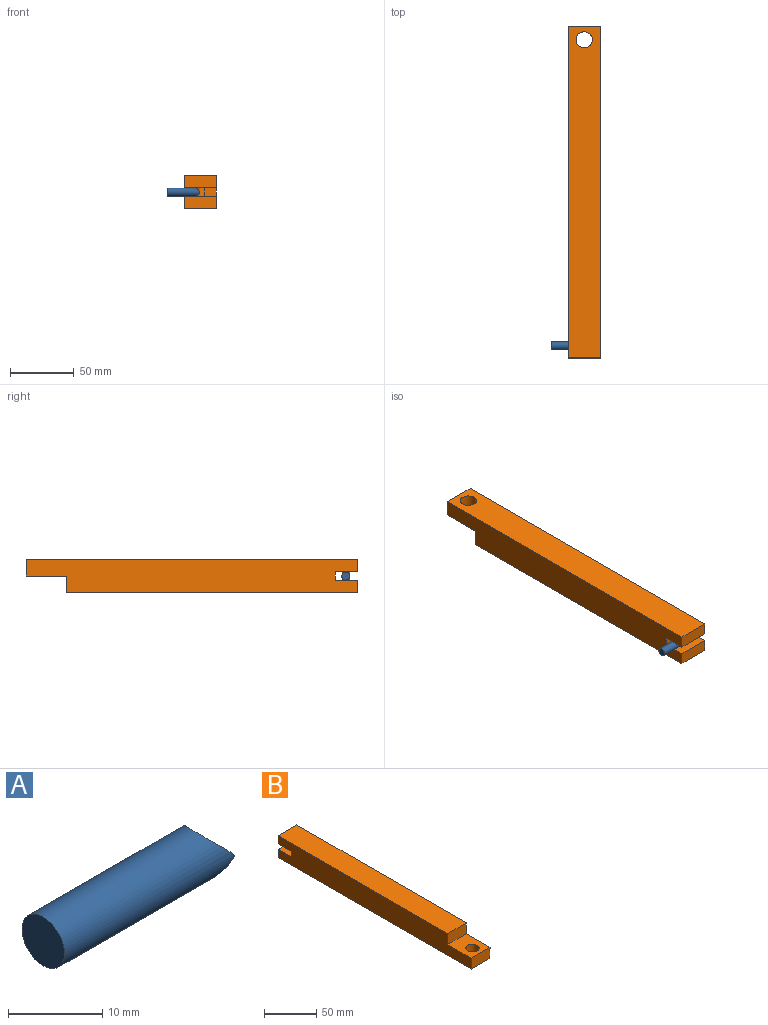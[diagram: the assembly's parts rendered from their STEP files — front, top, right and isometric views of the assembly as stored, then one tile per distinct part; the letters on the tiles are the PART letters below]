
ASSEMBLY  parts=2 mates=1
PART A: 5 faces, bbox 25.4x6.4x6.4 mm
  f0: plane 0.4x0.01mm, normal (1,0,0), area 0mm2, adj f1,f4
  f1: cylinder r=3.17mm len=25.4mm, axis (-1,0,0), area 470.3mm2, adj f0,f2,f3,f4
  f2: plane 0.4x0.01mm, normal (1,0,0), area 0mm2, adj f1,f4
  f3: plane 6.35x6.35mm, normal (-1,0,0), area 31.7mm2, adj f1
  f4: cylinder r=3.17mm len=6.35mm, axis (0,0,1), area 40.2mm2, adj f0,f1,f2
PART B: 14 faces, bbox 25.4x260.4x25.4 mm
  f0: plane 228.6x25.4mm, normal (0,0,1), area 5806.4mm2, adj f1,f2,f4,f10
  f1: plane 260.35x25.4mm, normal (1,0,0), area 6097.7mm2, adj f0,f3,f4,f5,f6,f7,f8,f9
  f2: plane 260.35x25.4mm, normal (-1,0,0), area 6097.7mm2, adj f0,f3,f4,f5,f6,f7,f8,f9
  f3: plane 25.4x17.64mm, normal (0,0,-1), area 416.3mm2, adj f1,f2,f4,f9,f12
  f4: plane 25.4x9.53mm, normal (0,1,0), area 241.9mm2, adj f0,f1,f2,f3
  f5: plane 25.4x12.7mm, normal (0,-1,0), area 322.6mm2, adj f1,f2,f6,f11
  f6: plane 260.35x25.4mm, normal (0,0,-1), area 6486.2mm2, adj f1,f2,f5,f7,f13
  f7: plane 25.4x9.53mm, normal (0,1,0), area 241.9mm2, adj f1,f2,f6,f8
  f8: plane 25.4x17.64mm, normal (0,0,1), area 416.3mm2, adj f1,f2,f7,f9,f12
  f9: plane 25.4x6.35mm, normal (0,1,0), area 161.3mm2, adj f1,f2,f3,f8
  f10: plane 25.4x12.7mm, normal (0,-1,0), area 322.6mm2, adj f0,f1,f2,f11
  f11: plane 31.75x25.4mm, normal (0,0,1), area 679.8mm2, adj f1,f2,f5,f10,f13
  f12: cylinder r=3.17mm len=6.35mm, axis (0,0,-1), area 126.7mm2, adj f3,f8
  f13: cylinder r=6.35mm len=12.7mm, axis (0,0,1), area 506.7mm2, adj f6,f11
PLACE A t=(-5.8,2.38,-2.4)mm
PLACE B rot(axis=(1,0,0),180deg) t=(7.1,253.21,10.35)mm
MATE revolute B.f12 <-> A.f4  axis (0,0,-1) through (19.8,2.38,0.83)mm
